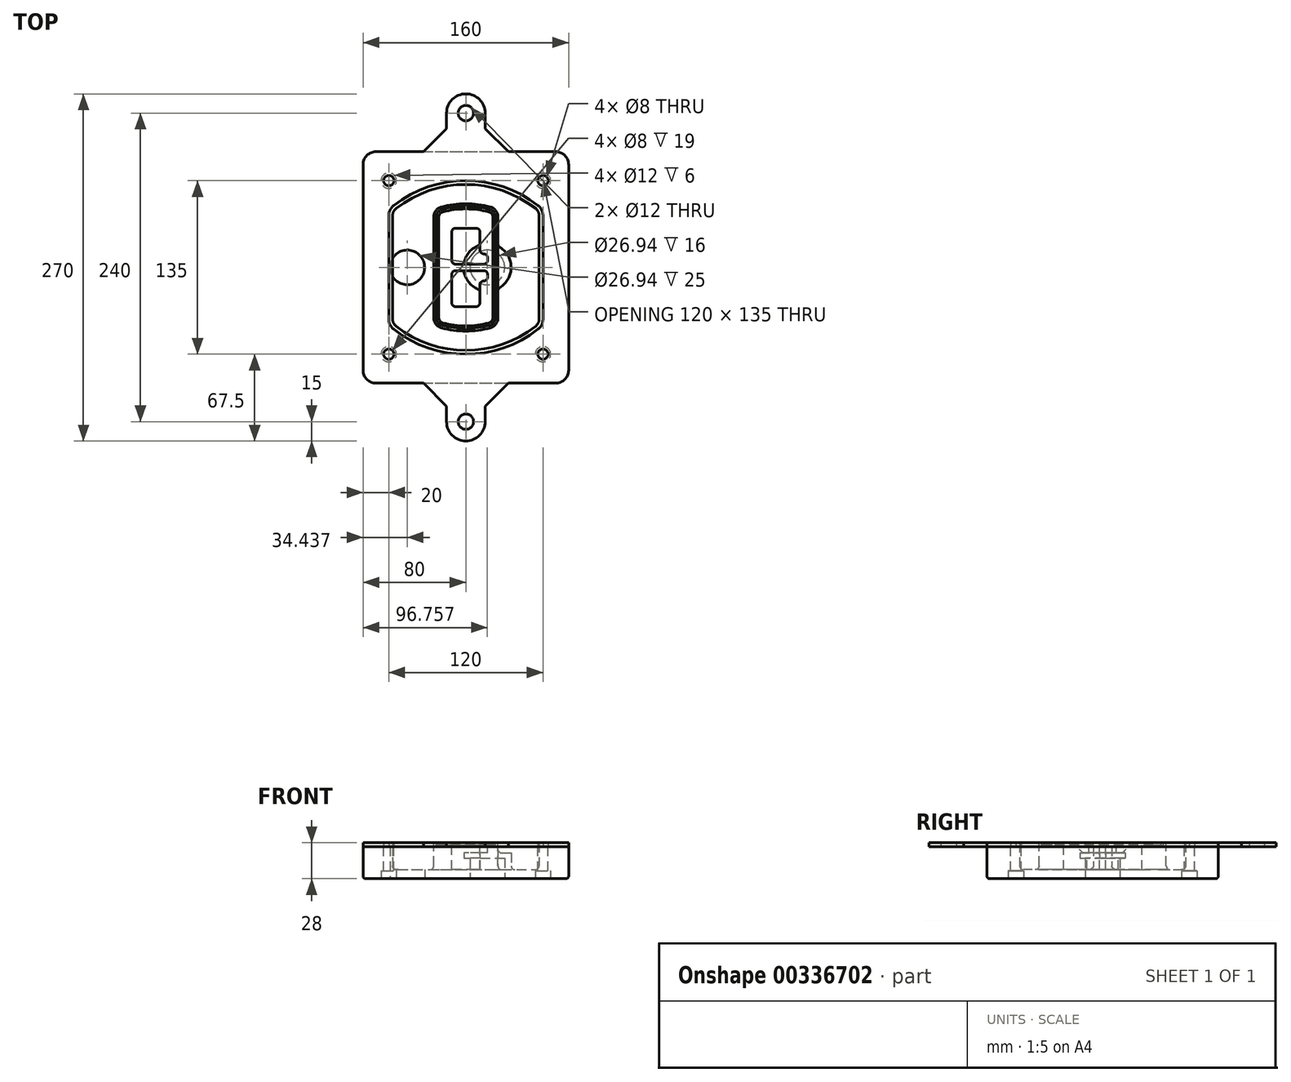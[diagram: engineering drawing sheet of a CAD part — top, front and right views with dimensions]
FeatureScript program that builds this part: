
annotation { "Feature Type Name" : "Feature", "Feature Type Description" : "" }
export const myFeature = defineFeature(function(context is Context, id is Id, definition is map)
    precondition{}
    {
        {
            var Q0;
            Q0=qCreatedBy(makeId("Top.planeOp"),FACE);
            var sketch = newSketch(context, id + "F0", { "sketchPlane" : qUnion([Q0])});
            skPoint(sketch, "E0.rect.middle", {"position": v(0, 0) * mm});
            skLineSegment(sketch, "E1.bottom", {"start": v(-70, -90) * mm, "end": v(70, -90) * mm});
            skLineSegment(sketch, "E1.top", {"start": v(-70, 90) * mm, "end": v(70, 90) * mm});
            skLineSegment(sketch, "E1.left", {"start": v(-80, -80) * mm, "end": v(-80, 80) * mm});
            skLineSegment(sketch, "E1.right", {"start": v(80, -80) * mm, "end": v(80, 80) * mm});
            skLineSegment(sketch, "E2", {"start": v(-80, 90) * mm, "end": v(80, -90) * mm, "construction": true});
            skLineSegment(sketch, "E3", {"start": v(80, 90) * mm, "end": v(-80, -90) * mm, "construction": true});
            skCircle(sketch, "E4", {"center": v(-60, 67.5) * mm, "radius": 4 * mm});
            skCircle(sketch, "E5", {"center": v(60, 67.5) * mm, "radius": 4 * mm});
            skCircle(sketch, "E6", {"center": v(60, -67.5) * mm, "radius": 4 * mm});
            skCircle(sketch, "E7", {"center": v(-60, -67.5) * mm, "radius": 4 * mm});
            skLineSegment(sketch, "E8", {"start": v(-60, 67.5) * mm, "end": v(60, 67.5) * mm, "construction": true});
            skLineSegment(sketch, "E9", {"start": v(60, 67.5) * mm, "end": v(60, -67.5) * mm, "construction": true});
            skLineSegment(sketch, "E10", {"start": v(60, -67.5) * mm, "end": v(-60, -67.5) * mm, "construction": true});
            skLineSegment(sketch, "E11", {"start": v(-60, -67.5) * mm, "end": v(-60, 67.5) * mm, "construction": true});
            skLineSegment(sketch, "E12", {"start": v(-60, 40.3) * mm, "end": v(-60, -40.3) * mm});
            skLineSegment(sketch, "E13", {"start": v(60, 40.3) * mm, "end": v(60, -40.3) * mm});
            skArc(sketch, "E14", {"start": v(56.15, 48.18) * mm, "mid": v(0, 67.5) * mm, "end": v(-56.15, 48.18) * mm});
            skArc(sketch, "E15", {"start": v(-56.15, -48.18) * mm, "mid": v(0, -67.5) * mm, "end": v(56.15, -48.18) * mm});
            skLineSegment(sketch, "E16", {"start": v(-60, 0) * mm, "end": v(60, 0) * mm, "construction": true});
            skPoint(sketch, "E17.visualSharp", {"position": v(-60, -45) * mm});
            skArc(sketch, "E17.filletArc", {"start": v(-60, -40.3) * mm, "mid": v(-58.99, -44.68) * mm, "end": v(-56.15, -48.18) * mm});
            skPoint(sketch, "E18.visualSharp", {"position": v(-60, 45) * mm});
            skArc(sketch, "E18.filletArc", {"start": v(-56.15, 48.18) * mm, "mid": v(-58.99, 44.68) * mm, "end": v(-60, 40.3) * mm});
            skPoint(sketch, "E19.visualSharp", {"position": v(60, 45) * mm});
            skArc(sketch, "E19.filletArc", {"start": v(60, 40.3) * mm, "mid": v(58.99, 44.68) * mm, "end": v(56.15, 48.18) * mm});
            skPoint(sketch, "E20.visualSharp", {"position": v(60, -45) * mm});
            skArc(sketch, "E20.filletArc", {"start": v(56.15, -48.18) * mm, "mid": v(58.99, -44.68) * mm, "end": v(60, -40.3) * mm});
            skPoint(sketch, "E21.visualSharp", {"position": v(-80, 90) * mm});
            skArc(sketch, "E21.filletArc", {"start": v(-70, 90) * mm, "mid": v(-77.07, 87.07) * mm, "end": v(-80, 80) * mm});
            skPoint(sketch, "E22.visualSharp", {"position": v(80, 90) * mm});
            skArc(sketch, "E22.filletArc", {"start": v(80, 80) * mm, "mid": v(77.07, 87.07) * mm, "end": v(70, 90) * mm});
            skPoint(sketch, "E23.visualSharp", {"position": v(80, -90) * mm});
            skArc(sketch, "E23.filletArc", {"start": v(70, -90) * mm, "mid": v(77.07, -87.07) * mm, "end": v(80, -80) * mm});
            skPoint(sketch, "E24.visualSharp", {"position": v(-80, -90) * mm});
            skArc(sketch, "E24.filletArc", {"start": v(-80, -80) * mm, "mid": v(-77.07, -87.07) * mm, "end": v(-70, -90) * mm});
            skArc(sketch, "E25.0", {"start": v(57, 40.3) * mm, "mid": v(56.3, 43.36) * mm, "end": v(54.3, 45.81) * mm});
            skLineSegment(sketch, "E25.1", {"start": v(57, 40.3) * mm, "end": v(57, -40.3) * mm});
            skArc(sketch, "E25.2", {"start": v(54.3, -45.81) * mm, "mid": v(56.3, -43.36) * mm, "end": v(57, -40.3) * mm});
            skArc(sketch, "E25.3", {"start": v(-54.3, -45.81) * mm, "mid": v(0, -64.5) * mm, "end": v(54.3, -45.81) * mm});
            skArc(sketch, "E25.4", {"start": v(-57, -40.3) * mm, "mid": v(-56.3, -43.36) * mm, "end": v(-54.3, -45.81) * mm});
            skArc(sketch, "E25.5", {"start": v(54.3, 45.81) * mm, "mid": v(0, 64.5) * mm, "end": v(-54.3, 45.81) * mm});
            skLineSegment(sketch, "E25.6", {"start": v(-57, 40.3) * mm, "end": v(-57, -40.3) * mm});
            skArc(sketch, "E25.7", {"start": v(-54.3, 45.81) * mm, "mid": v(-56.3, 43.36) * mm, "end": v(-57, 40.3) * mm});
            skArc(sketch, "E26.0", {"start": v(-58.62, 51.33) * mm, "mid": v(-62.58, 46.43) * mm, "end": v(-64, 40.3) * mm});
            skArc(sketch, "E26.1", {"start": v(58.62, 51.33) * mm, "mid": v(0, 71.5) * mm, "end": v(-58.62, 51.33) * mm});
            skArc(sketch, "E26.2", {"start": v(64, 40.3) * mm, "mid": v(62.58, 46.43) * mm, "end": v(58.62, 51.33) * mm});
            skLineSegment(sketch, "E26.3", {"start": v(64, 40.3) * mm, "end": v(64, -40.3) * mm});
            skArc(sketch, "E26.4", {"start": v(58.62, -51.33) * mm, "mid": v(62.58, -46.43) * mm, "end": v(64, -40.3) * mm});
            skLineSegment(sketch, "E26.5", {"start": v(-64, 40.3) * mm, "end": v(-64, -40.3) * mm});
            skArc(sketch, "E26.6", {"start": v(-58.62, -51.33) * mm, "mid": v(0, -71.5) * mm, "end": v(58.62, -51.33) * mm});
            skArc(sketch, "E26.7", {"start": v(-64, -40.3) * mm, "mid": v(-62.58, -46.43) * mm, "end": v(-58.62, -51.33) * mm});
            skSolve(sketch);
        }
        {
            var Q0;
            Q0=makeQuery(id+"F0.imprint","IMPRINT",FACE,{"disambiguationData":[TD([[makeQuery(id+"F0.imprint","IMPRINT",EDGE,{"derivedFrom":sQuery(id+"F0.wireOp",EDGE,"E1.bottom")}),1.0]])]});
            var Q1;
            Q1=makeQuery(id+"F0.imprint","IMPRINT",FACE,{"disambiguationData":[TD([[makeQuery(id+"F0.imprint","IMPRINT",EDGE,{"derivedFrom":sQuery(id+"F0.wireOp",EDGE,"E12")}),1.0]])]});
            var Q2;
            Q2=makeQuery(id+"F0.imprint","IMPRINT",FACE,{"disambiguationData":[TD([[makeQuery(id+"F0.imprint","IMPRINT",EDGE,{"derivedFrom":sQuery(id+"F0.wireOp",EDGE,"E25.0")}),1.0]])]});
            var Q3;
            Q3=makeQuery(id+"F0.imprint","IMPRINT",FACE,{"disambiguationData":[TD([[makeQuery(id+"F0.imprint","IMPRINT",EDGE,{"derivedFrom":sQuery(id+"F0.wireOp",EDGE,"E12")}),-1.0]])]});
            extrude(context, id + "F1", {"entities" : qUnion([Q0, Q1, Q2, Q3]), "oppositeDirection" : true, "depth" : 25 * mm});
        }
        {
            var Q0;
            Q0=makeQuery(id+"F0.imprint","IMPRINT",FACE,{"disambiguationData":[TD([[makeQuery(id+"F0.imprint","IMPRINT",EDGE,{"derivedFrom":sQuery(id+"F0.wireOp",EDGE,"E12")}),1.0]])]});
            extrude(context, id + "F2", {"entities" : qUnion([Q0]), "operationType" : NewBodyOperationType.ADD, "depth" : 3 * mm});
        }
        {
            var Q0;
            Q0=makeQuery(id+"F0.imprint","IMPRINT",FACE,{"disambiguationData":[TD([[makeQuery(id+"F0.imprint","IMPRINT",EDGE,{"derivedFrom":sQuery(id+"F0.wireOp",EDGE,"E25.0")}),1.0]])]});
            extrude(context, id + "F3", {"entities" : qUnion([Q0]), "operationType" : NewBodyOperationType.REMOVE, "oppositeDirection" : true, "depth" : 18 * mm});
        }
        {
            var Q0;
            Q0=makeQuery(id+"F2.opExtrude","CAP_FACE",FACE,{"disambiguationData":[OSD([sQuery(id+"F0.wireOp",EDGE,"E12"),sQuery(id+"F0.wireOp",EDGE,"E13"),sQuery(id+"F0.wireOp",EDGE,"E14"),sQuery(id+"F0.wireOp",EDGE,"E15"),sQuery(id+"F0.wireOp",EDGE,"E17.filletArc"),sQuery(id+"F0.wireOp",EDGE,"E18.filletArc"),sQuery(id+"F0.wireOp",EDGE,"E19.filletArc"),sQuery(id+"F0.wireOp",EDGE,"E20.filletArc"),sQuery(id+"F0.wireOp",EDGE,"E25.0"),sQuery(id+"F0.wireOp",EDGE,"E25.1"),sQuery(id+"F0.wireOp",EDGE,"E25.2"),sQuery(id+"F0.wireOp",EDGE,"E25.3"),sQuery(id+"F0.wireOp",EDGE,"E25.4"),sQuery(id+"F0.wireOp",EDGE,"E25.5"),sQuery(id+"F0.wireOp",EDGE,"E25.6"),sQuery(id+"F0.wireOp",EDGE,"E25.7")])],"isStart":false});
            var sketch = newSketch(context, id + "F4", { "sketchPlane" : qUnion([Q0])});
            skArc(sketch, "E27.0", {"start": v(-19.08, -46.97) * mm, "mid": v(0, -49.5) * mm, "end": v(19.08, -46.97) * mm});
            skArc(sketch, "E28.0", {"start": v(19.08, 46.97) * mm, "mid": v(0, 49.5) * mm, "end": v(-19.08, 46.97) * mm});
            skLineSegment(sketch, "E29", {"start": v(-25, 39.25) * mm, "end": v(-25, -39.25) * mm});
            skLineSegment(sketch, "E30", {"start": v(25, 39.25) * mm, "end": v(25, -39.25) * mm});
            skLineSegment(sketch, "E31", {"start": v(-25, 45.1) * mm, "end": v(25, 45.1) * mm, "construction": true});
            skLineSegment(sketch, "E32", {"start": v(-25, -45.1) * mm, "end": v(25, -45.1) * mm, "construction": true});
            skPoint(sketch, "E33.visualSharp", {"position": v(-25, 45.1) * mm});
            skArc(sketch, "E33.filletArc", {"start": v(-19.08, 46.97) * mm, "mid": v(-23.35, 44.11) * mm, "end": v(-25, 39.25) * mm});
            skPoint(sketch, "E34.visualSharp", {"position": v(25, 45.1) * mm});
            skArc(sketch, "E34.filletArc", {"start": v(25, 39.25) * mm, "mid": v(23.35, 44.11) * mm, "end": v(19.08, 46.97) * mm});
            skPoint(sketch, "E35.visualSharp", {"position": v(25, -45.1) * mm});
            skArc(sketch, "E35.filletArc", {"start": v(19.08, -46.97) * mm, "mid": v(23.35, -44.11) * mm, "end": v(25, -39.25) * mm});
            skPoint(sketch, "E36.visualSharp", {"position": v(-25, -45.1) * mm});
            skArc(sketch, "E36.filletArc", {"start": v(-25, -39.25) * mm, "mid": v(-23.35, -44.11) * mm, "end": v(-19.08, -46.97) * mm});
            skArc(sketch, "E37.0", {"start": v(54.3, 45.81) * mm, "mid": v(0, 64.5) * mm, "end": v(-54.3, 45.81) * mm});
            skArc(sketch, "E37.1", {"start": v(-54.3, 45.81) * mm, "mid": v(-56.3, 43.36) * mm, "end": v(-57, 40.3) * mm});
            skLineSegment(sketch, "E37.2", {"start": v(-57, 40.3) * mm, "end": v(-57, -40.3) * mm});
            skArc(sketch, "E37.3", {"start": v(-57, -40.3) * mm, "mid": v(-56.3, -43.36) * mm, "end": v(-54.3, -45.81) * mm});
            skArc(sketch, "E37.4", {"start": v(-54.3, -45.81) * mm, "mid": v(0, -64.5) * mm, "end": v(54.3, -45.81) * mm});
            skArc(sketch, "E37.5", {"start": v(54.3, -45.81) * mm, "mid": v(56.3, -43.36) * mm, "end": v(57, -40.3) * mm});
            skLineSegment(sketch, "E37.6", {"start": v(57, 40.3) * mm, "end": v(57, -40.3) * mm});
            skArc(sketch, "E37.7", {"start": v(57, 40.3) * mm, "mid": v(56.3, 43.36) * mm, "end": v(54.3, 45.81) * mm});
            skLineSegment(sketch, "E38.0", {"start": v(23, 39.25) * mm, "end": v(23, -39.25) * mm});
            skArc(sketch, "E38.1", {"start": v(18.56, -45.04) * mm, "mid": v(21.76, -42.9) * mm, "end": v(23, -39.25) * mm});
            skArc(sketch, "E38.2", {"start": v(-18.56, -45.04) * mm, "mid": v(0, -47.5) * mm, "end": v(18.56, -45.04) * mm});
            skArc(sketch, "E38.3", {"start": v(-23, -39.25) * mm, "mid": v(-21.76, -42.9) * mm, "end": v(-18.56, -45.04) * mm});
            skLineSegment(sketch, "E38.4", {"start": v(-23, 39.25) * mm, "end": v(-23, -39.25) * mm});
            skArc(sketch, "E38.5", {"start": v(23, 39.25) * mm, "mid": v(21.76, 42.9) * mm, "end": v(18.56, 45.04) * mm});
            skArc(sketch, "E38.6", {"start": v(-18.56, 45.04) * mm, "mid": v(-21.76, 42.9) * mm, "end": v(-23, 39.25) * mm});
            skArc(sketch, "E38.7", {"start": v(18.56, 45.04) * mm, "mid": v(0, 47.5) * mm, "end": v(-18.56, 45.04) * mm});
            skArc(sketch, "E39.0", {"start": v(21, 39.25) * mm, "mid": v(20.18, 41.68) * mm, "end": v(18.04, 43.1) * mm});
            skLineSegment(sketch, "E39.1", {"start": v(21, 39.25) * mm, "end": v(21, -39.25) * mm});
            skArc(sketch, "E39.2", {"start": v(18.04, -43.1) * mm, "mid": v(20.18, -41.68) * mm, "end": v(21, -39.25) * mm});
            skArc(sketch, "E39.3", {"start": v(-18.04, -43.1) * mm, "mid": v(0, -45.5) * mm, "end": v(18.04, -43.1) * mm});
            skArc(sketch, "E39.4", {"start": v(-21, -39.25) * mm, "mid": v(-20.18, -41.68) * mm, "end": v(-18.04, -43.1) * mm});
            skArc(sketch, "E39.5", {"start": v(18.04, 43.1) * mm, "mid": v(0, 45.5) * mm, "end": v(-18.04, 43.1) * mm});
            skLineSegment(sketch, "E39.6", {"start": v(-21, 39.25) * mm, "end": v(-21, -39.25) * mm});
            skArc(sketch, "E39.7", {"start": v(-18.04, 43.1) * mm, "mid": v(-20.18, 41.68) * mm, "end": v(-21, 39.25) * mm});
            skLineSegment(sketch, "E40", {"start": v(-25, 0) * mm, "end": v(25, 0) * mm, "construction": true});
            skLineSegment(sketch, "E41", {"start": v(-11, 5.5) * mm, "end": v(-11, 27.5) * mm});
            skLineSegment(sketch, "E42", {"start": v(-8, 30.5) * mm, "end": v(8, 30.5) * mm});
            skLineSegment(sketch, "E43", {"start": v(11, 27.5) * mm, "end": v(11, 13.5) * mm});
            skLineSegment(sketch, "E44", {"start": v(14, 10.5) * mm, "end": v(14, 10.5) * mm});
            skLineSegment(sketch, "E45", {"start": v(17, 7.5) * mm, "end": v(17, 5.5) * mm});
            skLineSegment(sketch, "E46", {"start": v(14, 2.5) * mm, "end": v(-8, 2.5) * mm});
            skPoint(sketch, "E47.visualSharp", {"position": v(-11, 30.5) * mm});
            skArc(sketch, "E47.filletArc", {"start": v(-8, 30.5) * mm, "mid": v(-10.12, 29.62) * mm, "end": v(-11, 27.5) * mm});
            skPoint(sketch, "E48.visualSharp", {"position": v(11, 30.5) * mm});
            skArc(sketch, "E48.filletArc", {"start": v(11, 27.5) * mm, "mid": v(10.12, 29.62) * mm, "end": v(8, 30.5) * mm});
            skPoint(sketch, "E49.visualSharp", {"position": v(11, 10.5) * mm});
            skArc(sketch, "E49.filletArc", {"start": v(11, 13.5) * mm, "mid": v(11.88, 11.38) * mm, "end": v(14, 10.5) * mm});
            skPoint(sketch, "E50.visualSharp", {"position": v(17, 10.5) * mm});
            skArc(sketch, "E50.filletArc", {"start": v(17, 7.5) * mm, "mid": v(16.12, 9.62) * mm, "end": v(14, 10.5) * mm});
            skPoint(sketch, "E51.visualSharp", {"position": v(17, 2.5) * mm});
            skArc(sketch, "E51.filletArc", {"start": v(14, 2.5) * mm, "mid": v(16.12, 3.38) * mm, "end": v(17, 5.5) * mm});
            skPoint(sketch, "E52.visualSharp", {"position": v(-11, 2.5) * mm});
            skArc(sketch, "E52.filletArc", {"start": v(-11, 5.5) * mm, "mid": v(-10.12, 3.38) * mm, "end": v(-8, 2.5) * mm});
            skLineSegment(sketch, "E53.0.MirrorCS", {"start": v(14, -2.5) * mm, "end": v(-8, -2.5) * mm});
            skArc(sketch, "E54.0.MirrorCS", {"start": v(-11, -5.5) * mm, "mid": v(-10.12, -3.38) * mm, "end": v(-8, -2.5) * mm});
            skLineSegment(sketch, "E55.0.MirrorCS", {"start": v(-11, -5.5) * mm, "end": v(-11, -27.5) * mm});
            skArc(sketch, "E56.0.MirrorCS", {"start": v(-8, -30.5) * mm, "mid": v(-10.12, -29.62) * mm, "end": v(-11, -27.5) * mm});
            skLineSegment(sketch, "E57.0.MirrorCS", {"start": v(-8, -30.5) * mm, "end": v(8, -30.5) * mm});
            skArc(sketch, "E58.0.MirrorCS", {"start": v(11, -27.5) * mm, "mid": v(10.12, -29.62) * mm, "end": v(8, -30.5) * mm});
            skLineSegment(sketch, "E59.0.MirrorCS", {"start": v(11, -27.5) * mm, "end": v(11, -13.5) * mm});
            skArc(sketch, "E60.0.MirrorCS", {"start": v(11, -13.5) * mm, "mid": v(11.88, -11.38) * mm, "end": v(14, -10.5) * mm});
            skArc(sketch, "E61.0.MirrorCS", {"start": v(17, -7.5) * mm, "mid": v(16.12, -9.62) * mm, "end": v(14, -10.5) * mm});
            skLineSegment(sketch, "E62.0.MirrorCS", {"start": v(17, -7.5) * mm, "end": v(17, -5.5) * mm});
            skArc(sketch, "E63.0.MirrorCS", {"start": v(14, -2.5) * mm, "mid": v(16.12, -3.38) * mm, "end": v(17, -5.5) * mm});
            skSolve(sketch);
        }
        {
            var Q0;
            Q0=makeQuery(id+"F4.imprint","IMPRINT",FACE,{"disambiguationData":[TD([[makeQuery(id+"F4.imprint","IMPRINT",EDGE,{"derivedFrom":sQuery(id+"F4.wireOp",EDGE,"E27.0")}),1.0]])]});
            var Q1;
            Q1=makeQuery(id+"F4.imprint","IMPRINT",FACE,{"disambiguationData":[TD([[makeQuery(id+"F4.imprint","IMPRINT",EDGE,{"derivedFrom":sQuery(id+"F4.wireOp",EDGE,"E38.0")}),-1.0]])]});
            var Q2;
            Q2=makeQuery(id+"F4.imprint","IMPRINT",FACE,{"disambiguationData":[TD([[makeQuery(id+"F4.imprint","IMPRINT",EDGE,{"derivedFrom":sQuery(id+"F4.wireOp",EDGE,"E39.0")}),1.0]])]});
            extrude(context, id + "F5", {"entities" : qUnion([Q0, Q1, Q2]), "operationType" : NewBodyOperationType.ADD, "endBound" : BoundingType.UP_TO_NEXT, "oppositeDirection" : true, "depth" : 25 * mm});
        }
        {
            var Q0;
            Q0=makeQuery(id+"F4.imprint","IMPRINT",FACE,{"disambiguationData":[TD([[makeQuery(id+"F4.imprint","IMPRINT",EDGE,{"derivedFrom":sQuery(id+"F4.wireOp",EDGE,"E38.0")}),-1.0]])]});
            extrude(context, id + "F6", {"entities" : qUnion([Q0]), "operationType" : NewBodyOperationType.REMOVE, "oppositeDirection" : true, "depth" : 2 * mm});
        }
        {
            var Q0;
            Q0=makeQuery(id+"F1.opExtrude","CAP_FACE",FACE,{"disambiguationData":[OSD([sQuery(id+"F0.wireOp",EDGE,"E1.bottom"),sQuery(id+"F0.wireOp",EDGE,"E1.top"),sQuery(id+"F0.wireOp",EDGE,"E1.left"),sQuery(id+"F0.wireOp",EDGE,"E1.right"),sQuery(id+"F0.wireOp",EDGE,"E4"),sQuery(id+"F0.wireOp",EDGE,"E5"),sQuery(id+"F0.wireOp",EDGE,"E6"),sQuery(id+"F0.wireOp",EDGE,"E7"),sQuery(id+"F0.wireOp",EDGE,"E21.filletArc"),sQuery(id+"F0.wireOp",EDGE,"E22.filletArc"),sQuery(id+"F0.wireOp",EDGE,"E23.filletArc"),sQuery(id+"F0.wireOp",EDGE,"E24.filletArc")])],"isStart":false});
            var sketch = newSketch(context, id + "F7", { "sketchPlane" : qUnion([Q0])});
            skCircle(sketch, "E64", {"center": v(16.76, 0) * mm, "radius": 13.47 * mm});
            skCircle(sketch, "E65", {"center": v(-45.56, 0) * mm, "radius": 13.47 * mm});
            skLineSegment(sketch, "E66", {"start": v(80, 0) * mm, "end": v(-80, 0) * mm});
            skCircle(sketch, "E67", {"center": v(16.76, 0) * mm, "radius": 18.47 * mm});
            skCircle(sketch, "E68", {"center": v(60, -67.5) * mm, "radius": 6 * mm});
            skCircle(sketch, "E69", {"center": v(-60, -67.5) * mm, "radius": 6 * mm});
            skCircle(sketch, "E70", {"center": v(-60, 67.5) * mm, "radius": 6 * mm});
            skCircle(sketch, "E71", {"center": v(60, 67.5) * mm, "radius": 6 * mm});
            skSolve(sketch);
        }
        {
            var Q0;
            {var subQ1=sQuery(id+"F7.wireOp",EDGE,"E66");var subQ4=sQuery(id+"F7.wireOp",EDGE,"E64");var subQ6=makeQuery(id+"F7.imprint","INTERSECT",VERTEX,{"disambiguationData":[OD(0.0)],"derivedFrom":[subQ4,subQ1]});Q0=makeQuery(id+"F7.imprint","IMPRINT",FACE,{"disambiguationData":[TD([[makeQuery(id+"F7.imprint","IMPRINT",EDGE,{"disambiguationData":[TD([[subQ6,-1.0]])],"derivedFrom":subQ4}),-1.0]])]});}
            var Q1;
            {var subQ0=sQuery(id+"F7.wireOp",EDGE,"E66");var subQ1=sQuery(id+"F7.wireOp",EDGE,"E64");var subQ3=makeQuery(id+"F7.imprint","INTERSECT",VERTEX,{"disambiguationData":[OD(0.0)],"derivedFrom":[subQ1,subQ0]});Q1=makeQuery(id+"F7.imprint","IMPRINT",FACE,{"disambiguationData":[TD([[makeQuery(id+"F7.imprint","IMPRINT",EDGE,{"disambiguationData":[TD([[subQ3,-1.0]])],"derivedFrom":subQ1}),1.0]])]});}
            var Q2;
            {var subQ0=sQuery(id+"F7.wireOp",EDGE,"E66");var subQ1=sQuery(id+"F7.wireOp",EDGE,"E64");var subQ3=makeQuery(id+"F7.imprint","INTERSECT",VERTEX,{"disambiguationData":[OD(0.0)],"derivedFrom":[subQ1,subQ0]});Q2=makeQuery(id+"F7.imprint","IMPRINT",FACE,{"disambiguationData":[TD([[makeQuery(id+"F7.imprint","IMPRINT",EDGE,{"disambiguationData":[TD([[subQ3,1.0]])],"derivedFrom":subQ1}),1.0]])]});}
            var Q3;
            {var subQ1=sQuery(id+"F7.wireOp",EDGE,"E66");var subQ4=sQuery(id+"F7.wireOp",EDGE,"E64");var subQ6=makeQuery(id+"F7.imprint","INTERSECT",VERTEX,{"disambiguationData":[OD(0.0)],"derivedFrom":[subQ4,subQ1]});Q3=makeQuery(id+"F7.imprint","IMPRINT",FACE,{"disambiguationData":[TD([[makeQuery(id+"F7.imprint","IMPRINT",EDGE,{"disambiguationData":[TD([[subQ6,1.0]])],"derivedFrom":subQ4}),-1.0]])]});}
            extrude(context, id + "F8", {"entities" : qUnion([Q0, Q1, Q2, Q3]), "operationType" : NewBodyOperationType.ADD, "oppositeDirection" : true, "depth" : 20 * mm});
        }
        {
            var Q0;
            {var subQ0=sQuery(id+"F7.wireOp",EDGE,"E66");var subQ1=sQuery(id+"F7.wireOp",EDGE,"E64");var subQ3=makeQuery(id+"F7.imprint","INTERSECT",VERTEX,{"disambiguationData":[OD(0.0)],"derivedFrom":[subQ1,subQ0]});Q0=makeQuery(id+"F7.imprint","IMPRINT",FACE,{"disambiguationData":[TD([[makeQuery(id+"F7.imprint","IMPRINT",EDGE,{"disambiguationData":[TD([[subQ3,-1.0]])],"derivedFrom":subQ1}),1.0]])]});}
            var Q1;
            {var subQ0=sQuery(id+"F7.wireOp",EDGE,"E66");var subQ1=sQuery(id+"F7.wireOp",EDGE,"E64");var subQ3=makeQuery(id+"F7.imprint","INTERSECT",VERTEX,{"disambiguationData":[OD(0.0)],"derivedFrom":[subQ1,subQ0]});Q1=makeQuery(id+"F7.imprint","IMPRINT",FACE,{"disambiguationData":[TD([[makeQuery(id+"F7.imprint","IMPRINT",EDGE,{"disambiguationData":[TD([[subQ3,1.0]])],"derivedFrom":subQ1}),1.0]])]});}
            extrude(context, id + "F9", {"entities" : qUnion([Q0, Q1]), "operationType" : NewBodyOperationType.REMOVE, "oppositeDirection" : true, "depth" : 16 * mm});
        }
        {
            var Q0;
            {var subQ0=sQuery(id+"F7.wireOp",EDGE,"E66");var subQ1=sQuery(id+"F7.wireOp",EDGE,"E65");var subQ3=makeQuery(id+"F7.imprint","INTERSECT",VERTEX,{"disambiguationData":[OD(0.0)],"derivedFrom":[subQ1,subQ0]});Q0=makeQuery(id+"F7.imprint","IMPRINT",FACE,{"disambiguationData":[TD([[makeQuery(id+"F7.imprint","IMPRINT",EDGE,{"disambiguationData":[TD([[subQ3,-1.0]])],"derivedFrom":subQ1}),1.0]])]});}
            var Q1;
            {var subQ0=sQuery(id+"F7.wireOp",EDGE,"E66");var subQ1=sQuery(id+"F7.wireOp",EDGE,"E65");var subQ3=makeQuery(id+"F7.imprint","INTERSECT",VERTEX,{"disambiguationData":[OD(0.0)],"derivedFrom":[subQ1,subQ0]});Q1=makeQuery(id+"F7.imprint","IMPRINT",FACE,{"disambiguationData":[TD([[makeQuery(id+"F7.imprint","IMPRINT",EDGE,{"disambiguationData":[TD([[subQ3,1.0]])],"derivedFrom":subQ1}),1.0]])]});}
            extrude(context, id + "F10", {"entities" : qUnion([Q0, Q1]), "operationType" : NewBodyOperationType.REMOVE, "oppositeDirection" : true, "depth" : 25 * mm});
        }
        {
            var Q0;
            Q0=makeQuery(id+"F7.imprint","IMPRINT",FACE,{"disambiguationData":[TD([[makeQuery(id+"F7.imprint","IMPRINT",EDGE,{"derivedFrom":sQuery(id+"F7.wireOp",EDGE,"E68")}),1.0]])]});
            var Q1;
            Q1=makeQuery(id+"F7.imprint","IMPRINT",FACE,{"disambiguationData":[TD([[makeQuery(id+"F7.imprint","IMPRINT",EDGE,{"derivedFrom":makeQuery(id+"F1.opExtrude","CAP_EDGE",EDGE,{"disambiguationData":[OSD([sQuery(id+"F0.wireOp",EDGE,"E5")])],"isStart":false})}),-1.0]])]});
            var Q2;
            Q2=makeQuery(id+"F7.imprint","IMPRINT",FACE,{"disambiguationData":[TD([[makeQuery(id+"F7.imprint","IMPRINT",EDGE,{"derivedFrom":sQuery(id+"F7.wireOp",EDGE,"E69")}),1.0]])]});
            var Q3;
            Q3=makeQuery(id+"F7.imprint","IMPRINT",FACE,{"disambiguationData":[TD([[makeQuery(id+"F7.imprint","IMPRINT",EDGE,{"derivedFrom":makeQuery(id+"F1.opExtrude","CAP_EDGE",EDGE,{"disambiguationData":[OSD([sQuery(id+"F0.wireOp",EDGE,"E4")])],"isStart":false})}),-1.0]])]});
            var Q4;
            Q4=makeQuery(id+"F7.imprint","IMPRINT",FACE,{"disambiguationData":[TD([[makeQuery(id+"F7.imprint","IMPRINT",EDGE,{"derivedFrom":sQuery(id+"F7.wireOp",EDGE,"E70")}),1.0]])]});
            var Q5;
            Q5=makeQuery(id+"F7.imprint","IMPRINT",FACE,{"disambiguationData":[TD([[makeQuery(id+"F7.imprint","IMPRINT",EDGE,{"derivedFrom":makeQuery(id+"F1.opExtrude","CAP_EDGE",EDGE,{"disambiguationData":[OSD([sQuery(id+"F0.wireOp",EDGE,"E7")])],"isStart":false})}),-1.0]])]});
            var Q6;
            Q6=makeQuery(id+"F7.imprint","IMPRINT",FACE,{"disambiguationData":[TD([[makeQuery(id+"F7.imprint","IMPRINT",EDGE,{"derivedFrom":sQuery(id+"F7.wireOp",EDGE,"E71")}),1.0]])]});
            var Q7;
            Q7=makeQuery(id+"F7.imprint","IMPRINT",FACE,{"disambiguationData":[TD([[makeQuery(id+"F7.imprint","IMPRINT",EDGE,{"derivedFrom":makeQuery(id+"F1.opExtrude","CAP_EDGE",EDGE,{"disambiguationData":[OSD([sQuery(id+"F0.wireOp",EDGE,"E6")])],"isStart":false})}),-1.0]])]});
            extrude(context, id + "F11", {"entities" : qUnion([Q0, Q1, Q2, Q3, Q4, Q5, Q6, Q7]), "operationType" : NewBodyOperationType.REMOVE, "oppositeDirection" : true, "depth" : 6 * mm});
        }
        {
            var Q0;
            Q0=makeQuery(id+"F9.boolean.opBoolean","COPY",FACE,{"derivedFrom":makeQuery(id+"F9.opExtrude","CAP_FACE",FACE,{"disambiguationData":[OSD([sQuery(id+"F7.wireOp",EDGE,"E64")])],"isStart":false})});
            var sketch = newSketch(context, id + "F12", { "sketchPlane" : qUnion([Q0])});
            skArc(sketch, "E72.0", {"start": v(11, 17.55) * mm, "mid": v(2.57, 11.82) * mm, "end": v(-1.54, 2.5) * mm});
            skArc(sketch, "E72.1", {"start": v(-1.54, -2.5) * mm, "mid": v(2.57, -11.82) * mm, "end": v(11, -17.55) * mm});
            skLineSegment(sketch, "E73", {"start": v(-1.54, -2.5) * mm, "end": v(14, -2.5) * mm});
            skLineSegment(sketch, "E74.0", {"start": v(14, 2.5) * mm, "end": v(-1.54, 2.5) * mm});
            skArc(sketch, "E74.1", {"start": v(14, 2.5) * mm, "mid": v(16.12, 3.38) * mm, "end": v(17, 5.5) * mm});
            skLineSegment(sketch, "E74.2", {"start": v(17, 7.5) * mm, "end": v(17, 5.5) * mm});
            skArc(sketch, "E74.3", {"start": v(17, 7.5) * mm, "mid": v(16.12, 9.62) * mm, "end": v(14, 10.5) * mm});
            skArc(sketch, "E74.4", {"start": v(11, 13.5) * mm, "mid": v(11.88, 11.38) * mm, "end": v(14, 10.5) * mm});
            skLineSegment(sketch, "E74.5", {"start": v(11, 17.55) * mm, "end": v(11, 13.5) * mm});
            skLineSegment(sketch, "E74.7", {"start": v(14, -2.5) * mm, "end": v(-1.54, -2.5) * mm});
            skArc(sketch, "E74.8", {"start": v(14, -2.5) * mm, "mid": v(16.12, -3.38) * mm, "end": v(17, -5.5) * mm});
            skLineSegment(sketch, "E74.9", {"start": v(17, -7.5) * mm, "end": v(17, -5.5) * mm});
            skArc(sketch, "E74.10", {"start": v(17, -7.5) * mm, "mid": v(16.12, -9.62) * mm, "end": v(14, -10.5) * mm});
            skArc(sketch, "E74.11", {"start": v(11, -13.5) * mm, "mid": v(11.88, -11.38) * mm, "end": v(14, -10.5) * mm});
            skLineSegment(sketch, "E74.12", {"start": v(11, -17.55) * mm, "end": v(11, -13.5) * mm});
            skPoint(sketch, "E75.orphan", {"position": v(11, -27.5) * mm});
            skPoint(sketch, "E76.orphan", {"position": v(-8, -2.5) * mm});
            skPoint(sketch, "E77.orphan", {"position": v(-8, 2.5) * mm});
            skPoint(sketch, "E78.orphan", {"position": v(11, 27.5) * mm});
            skSolve(sketch);
        }
        {
            var Q0;
            {var subQ7=sQuery(id+"F12.wireOp",EDGE,"E72.0");var subQ14=sQuery(id+"F12.wireOp",EDGE,"E72.1");var subQ16=sQuery(id+"F12.wireOp",EDGE,"E74.1");var subQ18=sQuery(id+"F12.wireOp",EDGE,"E74.8");Q0=qUnion([makeQuery(id+"F12.imprint","IMPRINT",FACE,{"disambiguationData":[TD([[makeQuery(id+"F12.imprint","IMPRINT",EDGE,{"derivedFrom":subQ7}),1.0]])]}),makeQuery(id+"F12.imprint","IMPRINT",FACE,{"disambiguationData":[TD([[makeQuery(id+"F12.imprint","IMPRINT",EDGE,{"derivedFrom":subQ14}),1.0]])]}),makeQuery(id+"F12.imprint","IMPRINT",FACE,{"disambiguationData":[TD([[makeQuery(id+"F12.imprint","IMPRINT",EDGE,{"derivedFrom":subQ16}),1.0]])]}),makeQuery(id+"F12.imprint","IMPRINT",FACE,{"disambiguationData":[TD([[makeQuery(id+"F12.imprint","IMPRINT",EDGE,{"derivedFrom":subQ18}),-1.0]])]})]);}
            var Q1;
            Q1=makeQuery(id+"F5.boolean.opBoolean","SPLIT",FACE,{"disambiguationData":[TD([makeQuery(id+"F5.opExtrude","SWEPT_FACE",FACE,{"disambiguationData":[OSD([sQuery(id+"F4.wireOp",EDGE,"E41")])]})])],"derivedFrom":makeQuery(id+"F3.boolean.opBoolean","COPY",FACE,{"derivedFrom":makeQuery(id+"F3.opExtrude","CAP_FACE",FACE,{"disambiguationData":[OSD([sQuery(id+"F0.wireOp",EDGE,"E25.0"),sQuery(id+"F0.wireOp",EDGE,"E25.1"),sQuery(id+"F0.wireOp",EDGE,"E25.2"),sQuery(id+"F0.wireOp",EDGE,"E25.3"),sQuery(id+"F0.wireOp",EDGE,"E25.4"),sQuery(id+"F0.wireOp",EDGE,"E25.5"),sQuery(id+"F0.wireOp",EDGE,"E25.6"),sQuery(id+"F0.wireOp",EDGE,"E25.7")])],"isStart":false})})});
            extrude(context, id + "F13", {"entities" : qUnion([Q0]), "operationType" : NewBodyOperationType.REMOVE, "endBound" : BoundingType.UP_TO_SURFACE, "endBoundEntityFace" : qUnion([Q1]), "depth" : 25 * mm});
        }
        {
            var Q0;
            Q0=makeQuery(id+"F3.boolean.opBoolean","COPY",EDGE,{"derivedFrom":makeQuery(id+"F3.opExtrude","CAP_EDGE",EDGE,{"disambiguationData":[OSD([sQuery(id+"F0.wireOp",EDGE,"E25.6")])],"isStart":false})});
            var Q1;
            Q1=makeQuery(id+"F8.boolean.opBoolean","INTERSECT",EDGE,{"derivedFrom":[makeQuery(id+"F5.opExtrude","SWEPT_FACE",FACE,{"disambiguationData":[OSD([sQuery(id+"F4.wireOp",EDGE,"E30")])]}),makeQuery(id+"F8.opExtrude","CAP_FACE",FACE,{"disambiguationData":[OSD([sQuery(id+"F7.wireOp",EDGE,"E67")])],"isStart":false})]});
            var Q2;
            Q2=makeQuery(id+"F8.boolean.opBoolean","INTERSECT",EDGE,{"disambiguationData":[OD(1.0)],"derivedFrom":[makeQuery(id+"F5.opExtrude","SWEPT_FACE",FACE,{"disambiguationData":[OSD([sQuery(id+"F4.wireOp",EDGE,"E30")])]}),makeQuery(id+"F8.opExtrude","SWEPT_FACE",FACE,{"disambiguationData":[OSD([sQuery(id+"F7.wireOp",EDGE,"E67")])]})]});
            var Q3;
            {var subQ0=sQuery(id+"F4.wireOp",EDGE,"E30");Q3=makeQuery(id+"F8.boolean.opBoolean","SPLIT",EDGE,{"disambiguationData":[TD([makeQuery(id+"F5.opExtrude","SWEPT_FACE",FACE,{"disambiguationData":[OSD([sQuery(id+"F4.wireOp",EDGE,"E35.filletArc")])]})])],"derivedFrom":makeQuery(id+"F5.opExtrude","CAP_EDGE",EDGE,{"disambiguationData":[OSD([subQ0])],"isStart":false})});}
            var Q4;
            {var subQ0=sQuery(id+"F0.wireOp",EDGE,"E25.7");var subQ1=sQuery(id+"F0.wireOp",EDGE,"E25.1");var subQ2=sQuery(id+"F0.wireOp",EDGE,"E25.6");var subQ3=sQuery(id+"F0.wireOp",EDGE,"E25.5");var subQ4=sQuery(id+"F0.wireOp",EDGE,"E25.4");var subQ5=sQuery(id+"F0.wireOp",EDGE,"E25.0");var subQ6=sQuery(id+"F0.wireOp",EDGE,"E25.2");var subQ7=sQuery(id+"F0.wireOp",EDGE,"E25.3");Q4=makeQuery(id+"F8.boolean.opBoolean","INTERSECT",EDGE,{"derivedFrom":[makeQuery(id+"F5.boolean.opBoolean","SPLIT",FACE,{"disambiguationData":[TD([makeQuery(id+"F2.opExtrude","SWEPT_FACE",FACE,{"disambiguationData":[OSD([subQ5])]})])],"derivedFrom":makeQuery(id+"F3.boolean.opBoolean","COPY",FACE,{"derivedFrom":makeQuery(id+"F3.opExtrude","CAP_FACE",FACE,{"disambiguationData":[OSD([subQ5,subQ1,subQ6,subQ7,subQ4,subQ3,subQ2,subQ0])],"isStart":false})})}),makeQuery(id+"F8.opExtrude","SWEPT_FACE",FACE,{"disambiguationData":[OSD([sQuery(id+"F7.wireOp",EDGE,"E67")])]})]});}
            var Q5;
            Q5=makeQuery(id+"F8.boolean.opBoolean","INTERSECT",EDGE,{"disambiguationData":[OD(0.0)],"derivedFrom":[makeQuery(id+"F5.opExtrude","SWEPT_FACE",FACE,{"disambiguationData":[OSD([sQuery(id+"F4.wireOp",EDGE,"E30")])]}),makeQuery(id+"F8.opExtrude","SWEPT_FACE",FACE,{"disambiguationData":[OSD([sQuery(id+"F7.wireOp",EDGE,"E67")])]})]});
            fillet(context, id + "F14", {"entities" : qUnion([Q0, Q1, Q2, Q3, Q4, Q5]), "radius" : 3 * mm, "tangentPropagation" : true, "allowEdgeOverflow" : false});
        }
        {
            var Q0;
            Q0=makeQuery(id+"F1.opExtrude","CAP_EDGE",EDGE,{"disambiguationData":[OSD([sQuery(id+"F0.wireOp",EDGE,"E1.bottom")])],"isStart":false});
            fillet(context, id + "F15", {"entities" : qUnion([Q0]), "radius" : 2 * mm, "tangentPropagation" : true, "allowEdgeOverflow" : false});
        }
        {
            var Q0;
            {var subQ0=sQuery(id+"F0.wireOp",EDGE,"E21.filletArc");var subQ1=sQuery(id+"F0.wireOp",EDGE,"E7");var subQ2=sQuery(id+"F0.wireOp",EDGE,"E6");var subQ3=sQuery(id+"F0.wireOp",EDGE,"E5");var subQ4=sQuery(id+"F0.wireOp",EDGE,"E4");var subQ5=sQuery(id+"F0.wireOp",EDGE,"E22.filletArc");var subQ6=sQuery(id+"F0.wireOp",EDGE,"E1.bottom");var subQ7=sQuery(id+"F0.wireOp",EDGE,"E1.right");var subQ8=sQuery(id+"F0.wireOp",EDGE,"E1.top");var subQ9=sQuery(id+"F0.wireOp",EDGE,"E1.left");var subQ10=sQuery(id+"F0.wireOp",EDGE,"E23.filletArc");var subQ11=sQuery(id+"F0.wireOp",EDGE,"E24.filletArc");Q0=makeQuery(id+"F2.boolean.opBoolean","SPLIT",FACE,{"disambiguationData":[TD([makeQuery(id+"F1.opExtrude","SWEPT_FACE",FACE,{"disambiguationData":[OSD([subQ6])]})])],"derivedFrom":makeQuery(id+"F1.opExtrude","CAP_FACE",FACE,{"disambiguationData":[OSD([subQ6,subQ8,subQ9,subQ7,subQ4,subQ3,subQ2,subQ1,subQ0,subQ5,subQ10,subQ11])],"isStart":true})});}
            var sketch = newSketch(context, id + "F16", { "sketchPlane" : qUnion([Q0])});
            skLineSegment(sketch, "E79", {"start": v(0, 90) * mm, "end": v(0, 120) * mm, "construction": true});
            skCircle(sketch, "E80", {"center": v(0, 120) * mm, "radius": 6 * mm});
            skLineSegment(sketch, "E81", {"start": v(-33, 90) * mm, "end": v(-15, 108) * mm});
            skLineSegment(sketch, "E82", {"start": v(-15, 108) * mm, "end": v(-15, 120) * mm});
            skLineSegment(sketch, "E83", {"start": v(33, 90) * mm, "end": v(15, 108) * mm});
            skLineSegment(sketch, "E84", {"start": v(15, 108) * mm, "end": v(15, 120) * mm});
            skArc(sketch, "E85", {"start": v(15, 120) * mm, "mid": v(0, 135) * mm, "end": v(-15, 120) * mm});
            skLineSegment(sketch, "E86", {"start": v(-80, 0) * mm, "end": v(80, 0) * mm, "construction": true});
            skArc(sketch, "E87.MirrorCS", {"start": v(-15, 120) * mm, "mid": v(0, 135) * mm, "end": v(15, 120) * mm});
            skLineSegment(sketch, "E88.MirrorCS", {"start": v(33, -90) * mm, "end": v(15, -108) * mm});
            skLineSegment(sketch, "E89.MirrorCS", {"start": v(15, -108) * mm, "end": v(15, -120) * mm});
            skArc(sketch, "E90.MirrorCS", {"start": v(-15, -120) * mm, "mid": v(0, -135) * mm, "end": v(15, -120) * mm});
            skCircle(sketch, "E91.MirrorC", {"center": v(0, -120) * mm, "radius": 6 * mm});
            skLineSegment(sketch, "E92.MirrorCS", {"start": v(0, -90) * mm, "end": v(0, -120) * mm, "construction": true});
            skLineSegment(sketch, "E93.MirrorCS", {"start": v(-15, -108) * mm, "end": v(-15, -120) * mm});
            skLineSegment(sketch, "E94.MirrorCS", {"start": v(-33, -90) * mm, "end": v(-15, -108) * mm});
            skSolve(sketch);
        }
        {
            var Q0;
            Q0=makeQuery(id+"F16.imprint","IMPRINT",FACE,{"disambiguationData":[TD([[makeQuery(id+"F16.imprint","IMPRINT",EDGE,{"derivedFrom":makeQuery(id+"F1.opExtrude","CAP_EDGE",EDGE,{"disambiguationData":[OSD([sQuery(id+"F0.wireOp",EDGE,"E1.left")])],"isStart":true})}),-1.0]])]});
            var Q1;
            Q1=makeQuery(id+"F16.imprint","IMPRINT",FACE,{"disambiguationData":[TD([[makeQuery(id+"F16.imprint","IMPRINT",EDGE,{"derivedFrom":sQuery(id+"F16.wireOp",EDGE,"E84")}),1.0]])]});
            var Q2;
            {var subQ0=sQuery(id+"F16.wireOp",EDGE,"E88.MirrorCS");Q2=makeQuery(id+"F16.imprint","IMPRINT",FACE,{"disambiguationData":[TD([[makeQuery(id+"F16.imprint","IMPRINT",EDGE,{"derivedFrom":subQ0}),-1.0]])]});}
            var Q3;
            Q3=makeQuery(id+"F2.opExtrude","CAP_FACE",FACE,{"disambiguationData":[OSD([sQuery(id+"F0.wireOp",EDGE,"E12"),sQuery(id+"F0.wireOp",EDGE,"E13"),sQuery(id+"F0.wireOp",EDGE,"E14"),sQuery(id+"F0.wireOp",EDGE,"E15"),sQuery(id+"F0.wireOp",EDGE,"E17.filletArc"),sQuery(id+"F0.wireOp",EDGE,"E18.filletArc"),sQuery(id+"F0.wireOp",EDGE,"E19.filletArc"),sQuery(id+"F0.wireOp",EDGE,"E20.filletArc"),sQuery(id+"F0.wireOp",EDGE,"E25.0"),sQuery(id+"F0.wireOp",EDGE,"E25.1"),sQuery(id+"F0.wireOp",EDGE,"E25.2"),sQuery(id+"F0.wireOp",EDGE,"E25.3"),sQuery(id+"F0.wireOp",EDGE,"E25.4"),sQuery(id+"F0.wireOp",EDGE,"E25.5"),sQuery(id+"F0.wireOp",EDGE,"E25.6"),sQuery(id+"F0.wireOp",EDGE,"E25.7")])],"isStart":false});
            extrude(context, id + "F17", {"entities" : qUnion([Q0, Q1, Q2]), "endBound" : BoundingType.UP_TO_SURFACE, "endBoundEntityFace" : qUnion([Q3]), "depth" : 25 * mm});
        }
    });
